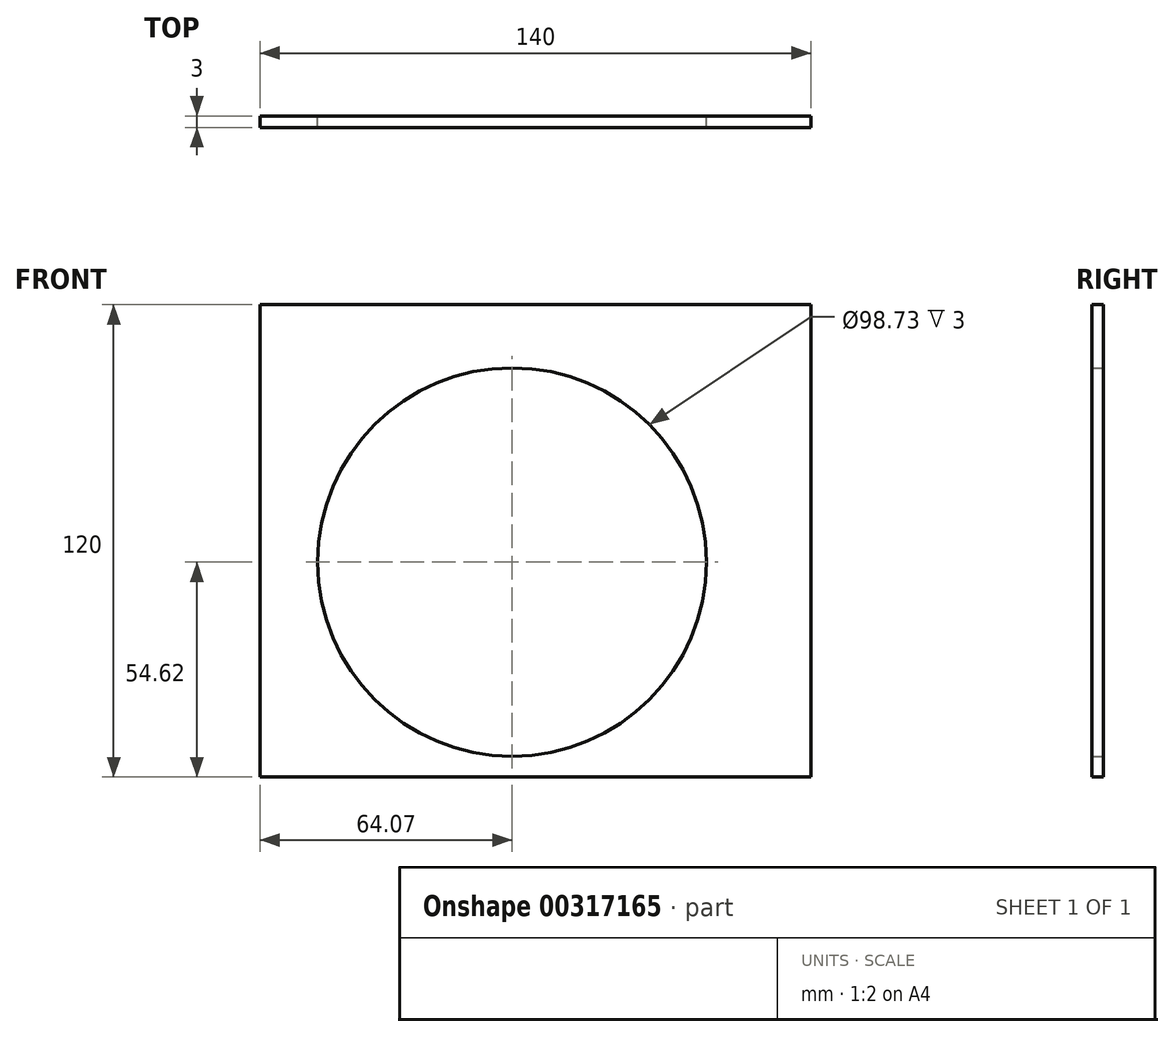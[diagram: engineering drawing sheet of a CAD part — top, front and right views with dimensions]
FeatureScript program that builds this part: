
annotation { "Feature Type Name" : "Feature", "Feature Type Description" : "" }
export const myFeature = defineFeature(function(context is Context, id is Id, definition is map)
    precondition{}
    {
        {
            var Q0;
            Q0=qCreatedBy(makeId("Front.planeOp"),FACE);
            var sketch = newSketch(context, id + "F0", { "sketchPlane" : qUnion([Q0])});
            skLineSegment(sketch, "E0.bottom", {"start": v(100, 65.38) * mm, "end": v(-100, 65.38) * mm});
            skLineSegment(sketch, "E0.top", {"start": v(100, -65.38) * mm, "end": v(-100, -65.38) * mm});
            skLineSegment(sketch, "E0.left", {"start": v(100, 65.38) * mm, "end": v(100, -65.38) * mm});
            skLineSegment(sketch, "E0.right", {"start": v(-100, 65.38) * mm, "end": v(-100, -65.38) * mm});
            skPoint(sketch, "E0.middle", {"position": v(0, 0) * mm});
            skCircle(sketch, "E1", {"center": v(0, 0) * mm, "radius": 49.37 * mm});
            skSolve(sketch);
        }
        {
            var Q0;
            Q0=qSketchRegion(id+"F0",true);
            extrude(context, id + "F1", {"entities" : qUnion([Q0]), "depth" : 3 * mm});
        }
        {
            var Q0;
            Q0=makeQuery(id+"F1.opExtrude","CAP_FACE",FACE,{"disambiguationData":[OSD([sQuery(id+"F0.wireOp",EDGE,"E0.bottom"),sQuery(id+"F0.wireOp",EDGE,"E0.top"),sQuery(id+"F0.wireOp",EDGE,"E0.left"),sQuery(id+"F0.wireOp",EDGE,"E0.right"),sQuery(id+"F0.wireOp",EDGE,"E1")])],"isStart":false});
            var sketch = newSketch(context, id + "F2", { "sketchPlane" : qUnion([Q0])});
            skLineSegment(sketch, "E2.bottom", {"start": v(-100, -65.38) * mm, "end": v(100, -65.38) * mm});
            skLineSegment(sketch, "E2.top", {"start": v(-100, -54.62) * mm, "end": v(100, -54.62) * mm});
            skLineSegment(sketch, "E2.left", {"start": v(-100, -65.38) * mm, "end": v(-100, -54.62) * mm});
            skLineSegment(sketch, "E2.right", {"start": v(100, -65.38) * mm, "end": v(100, -54.62) * mm});
            skSolve(sketch);
        }
        {
            var Q0;
            Q0 = qSketchRegion(id + "F2", true);
            extrude(context, id + "F3", {"entities" : qUnion([Q0]), "operationType" : NewBodyOperationType.REMOVE, "oppositeDirection" : true, "depth" : 25 * mm});
        }
        {
            var Q0;
            Q0=makeQuery(id+"F1.opExtrude","CAP_FACE",FACE,{"disambiguationData":[OSD([sQuery(id+"F0.wireOp",EDGE,"E0.bottom"),sQuery(id+"F0.wireOp",EDGE,"E0.top"),sQuery(id+"F0.wireOp",EDGE,"E0.left"),sQuery(id+"F0.wireOp",EDGE,"E0.right"),sQuery(id+"F0.wireOp",EDGE,"E1")])],"isStart":false});
            var sketch = newSketch(context, id + "F4", { "sketchPlane" : qUnion([Q0])});
            skLineSegment(sketch, "E3.bottom", {"start": v(-100, 65.38) * mm, "end": v(-64.07, 65.38) * mm});
            skLineSegment(sketch, "E3.top", {"start": v(-100, -54.62) * mm, "end": v(-64.07, -54.62) * mm});
            skLineSegment(sketch, "E3.left", {"start": v(-100, 65.38) * mm, "end": v(-100, -54.62) * mm});
            skLineSegment(sketch, "E3.right", {"start": v(-64.07, 65.38) * mm, "end": v(-64.07, -54.62) * mm});
            skLineSegment(sketch, "E4.bottom", {"start": v(100, 65.38) * mm, "end": v(75.93, 65.38) * mm});
            skLineSegment(sketch, "E4.top", {"start": v(100, -54.62) * mm, "end": v(75.93, -54.62) * mm});
            skLineSegment(sketch, "E4.left", {"start": v(100, 65.38) * mm, "end": v(100, -54.62) * mm});
            skLineSegment(sketch, "E4.right", {"start": v(75.93, 65.38) * mm, "end": v(75.93, -54.62) * mm});
            skSolve(sketch);
        }
        {
            var Q0;
            Q0 = qSketchRegion(id + "F4", true);
            extrude(context, id + "F5", {"entities" : qUnion([Q0]), "operationType" : NewBodyOperationType.REMOVE, "oppositeDirection" : true, "depth" : 25 * mm});
        }
    });
